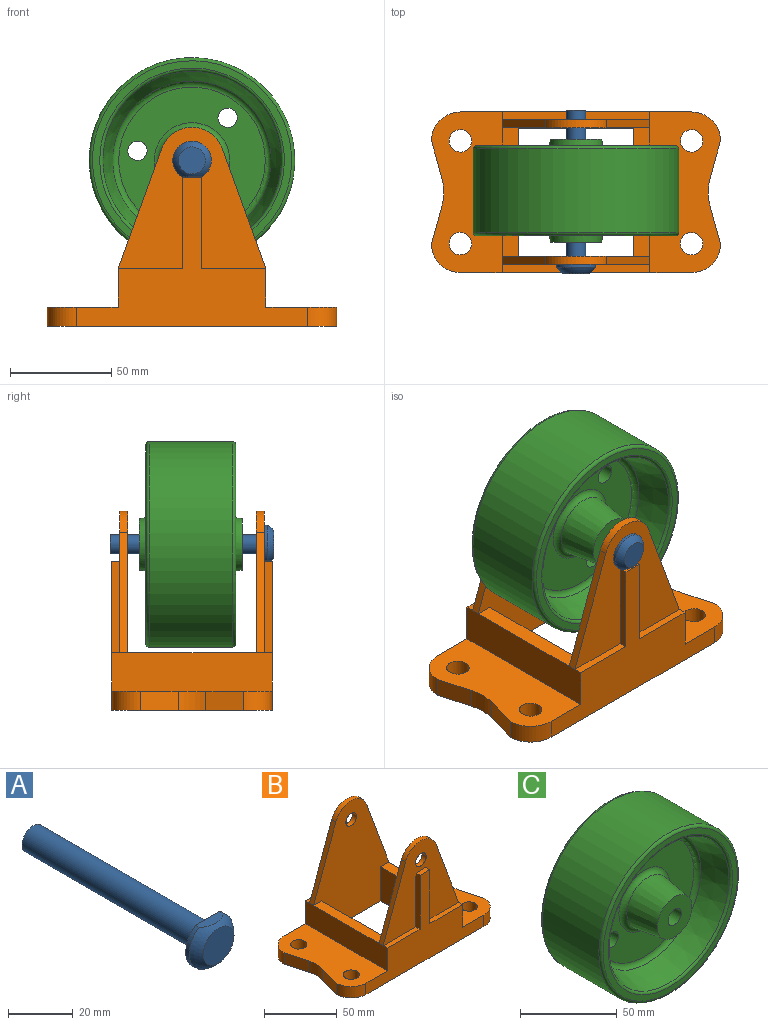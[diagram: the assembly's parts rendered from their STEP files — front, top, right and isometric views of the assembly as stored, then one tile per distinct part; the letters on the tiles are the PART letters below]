
ASSEMBLY  parts=3 mates=2
PART A: 7 faces, bbox 19.1x81x19.1 mm
  f0: cylinder r=9.53mm len=19.05mm, axis (0,1,0), area 77.3mm2, adj f3,f4,f6
  f1: plane 9.53x9.53mm, normal (0,1,0), area 71.3mm2, adj f2
  f2: cylinder r=4.76mm len=76.2mm, axis (0,1,0), area 2280.2mm2, adj f1,f3
  f3: plane 19.05x17.46mm, normal (0,1,0), area 202.4mm2, adj f0,f2,f6
  f4: sphere r=11.11mm, area 202.5mm2, adj f0,f5,f6
  f5: plane 13.31x13.31mm, normal (0,-1,0), area 139.2mm2, adj f4
  f6: plane 10.53x3.64mm, normal (0,0,1), area 31.6mm2, adj f0,f3,f4
PART B: 47 faces, bbox 142.9x79.4x98.4 mm
  f0: plane 142.88x79.38mm, normal (0,0,-1), area 6794.7mm2, adj f3,f4,f12,f13,f14,f15,f16,f17
  f1: plane 79.38x19.05mm, normal (-1,0,0), area 1512.1mm2, adj f8,f9,f10,f15,f21,f28,f40,f44
  f2: plane 79.38x19.05mm, normal (1,0,0), area 1512.1mm2, adj f6,f7,f11,f15,f21,f31,f41,f43
  f3: plane 98.43x73.03mm, normal (0,-1,0), area 4831.5mm2, adj f0,f7,f8,f29,f30,f39,f40,f41
  f4: plane 98.43x73.03mm, normal (0,1,0), area 4831.5mm2, adj f0,f7,f8,f29,f30,f43,f44,f45
  f5: plane 73.03x69.85mm, normal (0,1,0), area 2767.5mm2, adj f6,f10,f35,f36,f37,f39,f40,f41
  f6: plane 31.75x3.97mm, normal (0,0,1), area 126mm2, adj f2,f5,f15,f36
  f7: plane 63.5x7.94mm, normal (0,0,1), area 504mm2, adj f2,f3,f4,f30
  f8: plane 63.5x7.94mm, normal (0,0,1), area 504mm2, adj f1,f3,f4,f29
  f9: plane 31.75x3.97mm, normal (0,0,1), area 126mm2, adj f1,f21,f33,f38
  f10: plane 31.75x3.97mm, normal (0,0,1), area 126mm2, adj f1,f5,f15,f35
  f11: plane 79.38x34.93mm, normal (0,0,1), area 2313.7mm2, adj f2,f12,f13,f14,f15,f21,f22,f24
  f12: cylinder r=25.4mm len=13.75mm, axis (0,0,-1), area 132.7mm2, adj f0,f11,f13,f26
  f13: plane 18.52x9.53mm, normal (0.96,-0.27,0), area 183.3mm2, adj f0,f11,f12,f14
  f14: cylinder r=14.29mm len=14.29mm, axis (0,0,-1), area 213.8mm2, adj f0,f11,f13,f15
  f15: plane 114.3x73.82mm, normal (0,1,0), area 2910.8mm2, adj f0,f1,f2,f6,f10,f11,f14,f16
  f16: cylinder r=14.29mm len=14.29mm, axis (0,0,-1), area 213.8mm2, adj f0,f15,f17,f28
  f17: plane 18.52x9.53mm, normal (-0.96,-0.27,0), area 183.3mm2, adj f0,f16,f18,f28
  f18: cylinder r=25.4mm len=13.75mm, axis (0,0,-1), area 132.7mm2, adj f0,f17,f19,f28
  f19: plane 18.52x9.53mm, normal (-0.96,0.27,0), area 183.3mm2, adj f0,f18,f20,f28
  f20: cylinder r=14.29mm len=14.29mm, axis (0,0,-1), area 213.8mm2, adj f0,f19,f21,f28
  f21: plane 114.3x73.82mm, normal (0,-1,0), area 2910.8mm2, adj f0,f1,f2,f9,f11,f20,f22,f28
  f22: cylinder r=14.29mm len=14.29mm, axis (0,0,-1), area 213.8mm2, adj f0,f11,f21,f26
  f23: cylinder r=5.56mm len=11.11mm, axis (0,0,-1), area 332.5mm2, adj f0,f28
  f24: cylinder r=5.56mm len=11.11mm, axis (0,0,-1), area 332.5mm2, adj f0,f11
  f25: cylinder r=5.56mm len=11.11mm, axis (0,0,-1), area 332.5mm2, adj f0,f11
  f26: plane 18.52x9.53mm, normal (0.96,0.27,0), area 183.3mm2, adj f0,f11,f12,f22
  f27: cylinder r=5.56mm len=11.11mm, axis (0,0,-1), area 332.5mm2, adj f0,f28
  f28: plane 79.38x34.93mm, normal (0,0,1), area 2313.7mm2, adj f1,f15,f16,f17,f18,f19,f20,f21
  f29: plane 63.5x28.58mm, normal (1,0,0), area 1814.5mm2, adj f0,f3,f4,f8
  f30: plane 63.5x28.58mm, normal (-1,0,0), area 1814.5mm2, adj f0,f3,f4,f7
  f31: plane 31.75x3.97mm, normal (0,0,1), area 126mm2, adj f2,f21,f32,f38
  f32: plane 45.24x3.97mm, normal (1,0,0), area 179.6mm2, adj f21,f31,f34,f38
  f33: plane 45.24x3.97mm, normal (-1,0,0), area 179.6mm2, adj f9,f21,f34,f38
  f34: plane 9.53x3.97mm, normal (0,0,1), area 37.8mm2, adj f21,f32,f33,f38
  f35: plane 45.24x3.97mm, normal (-1,0,0), area 179.6mm2, adj f5,f10,f15,f37
  f36: plane 45.24x3.97mm, normal (1,0,0), area 179.6mm2, adj f5,f6,f15,f37
  f37: plane 9.53x3.97mm, normal (0,0,1), area 37.8mm2, adj f5,f15,f35,f36
  f38: plane 73.03x69.85mm, normal (0,-1,0), area 2767.5mm2, adj f9,f31,f32,f33,f34,f43,f44,f45
  f39: cylinder r=15.88mm len=29.84mm, axis (0,-1,0), area 154mm2, adj f3,f5,f40,f41
  f40: plane 59.4x21.59mm, normal (-0.94,0,0.34), area 250.8mm2, adj f1,f3,f5,f39
  f41: plane 59.4x21.59mm, normal (0.94,0,0.34), area 250.8mm2, adj f2,f3,f5,f39
  f42: cylinder r=5.16mm len=10.32mm, axis (0,-1,0), area 128.7mm2, adj f3,f5
  f43: plane 59.4x21.59mm, normal (0.94,0,0.34), area 250.8mm2, adj f2,f4,f38,f45
  f44: plane 59.4x21.59mm, normal (-0.94,0,0.34), area 250.8mm2, adj f1,f4,f38,f45
  f45: cylinder r=15.88mm len=29.84mm, axis (0,-1,0), area 154mm2, adj f4,f38,f43,f44
  f46: cylinder r=5.16mm len=10.32mm, axis (0,-1,0), area 128.7mm2, adj f4,f38
PART C: 23 faces, bbox 110x50.8x110 mm
  f0: plane 72.37x72.37mm, normal (0,-1,0), area 2809.3mm2, adj f1,f15,f20,f21,f22
  f1: torus R=18.63mm, axis (0,1,0), area 476.6mm2, adj f0,f2
  f2: cone r=12.7mm half-angle=8.1deg, axis (0,1,0), area 1744.1mm2, adj f1,f3
  f3: plane 25.4x25.4mm, normal (0,-1,0), area 433.5mm2, adj f2,f4
  f4: cylinder r=4.83mm len=50.8mm, axis (0,1,0), area 1540.4mm2, adj f3,f5
  f5: plane 25.4x25.4mm, normal (0,1,0), area 433.5mm2, adj f4,f6
  f6: cone r=12.7mm half-angle=8.1deg, axis (0,-1,0), area 1744.1mm2, adj f5,f7
  f7: torus R=18.63mm, axis (0,1,0), area 476.6mm2, adj f6,f8
  f8: plane 72.37x72.37mm, normal (0,1,0), area 2809.3mm2, adj f7,f9,f20,f21,f22
  f9: torus R=36.18mm, axis (0,1,0), area 960.6mm2, adj f8,f10
  f10: cone r=39.22mm half-angle=17.3deg, axis (0,1,0), area 4304.7mm2, adj f9,f16
  f11: plane 98.43x98.43mm, normal (0,1,0), area 1070.7mm2, adj f16,f17
  f12: cylinder r=50.8mm len=101.6mm, axis (0,1,0), area 13174.4mm2, adj f17,f18
  f13: plane 98.43x98.43mm, normal (0,-1,0), area 1070.7mm2, adj f18,f19
  f14: cone r=39.22mm half-angle=17.3deg, axis (0,-1,0), area 4304.7mm2, adj f15,f19
  f15: torus R=36.18mm, axis (0,1,0), area 960.6mm2, adj f0,f14
  f16: torus R=45.62mm, axis (0,-1,0), area 566.3mm2, adj f10,f11
  f17: torus R=49.21mm, axis (0,-1,0), area 786.9mm2, adj f11,f12
  f18: torus R=49.21mm, axis (0,-1,0), area 786.9mm2, adj f12,f13
  f19: torus R=45.62mm, axis (0,-1,0), area 566.3mm2, adj f13,f14
  f20: cylinder r=4.76mm len=9.53mm, axis (0,-1,0), area 190mm2, adj f0,f8
  f21: cylinder r=4.76mm len=9.53mm, axis (0,-1,0), area 190mm2, adj f0,f8
  f22: cylinder r=4.76mm len=9.53mm, axis (0,-1,0), area 190mm2, adj f0,f8
PLACE A rot(axis=(0,1,0),178.8deg) t=(91.22,48.21,12.56)mm
PLACE B t=(50.73,64.16,-69.51)mm fixed
PLACE C rot(axis=(0,1,0),39.9deg) t=(91.22,51.11,12.56)mm
MATE revolute A.f0 <-> C.f1  axis (0,1,0) through (91.22,52.88,12.56)mm
MATE revolute A.f3 <-> B.f39  axis (0,1,0) through (91.21,14.78,13.04)mm
